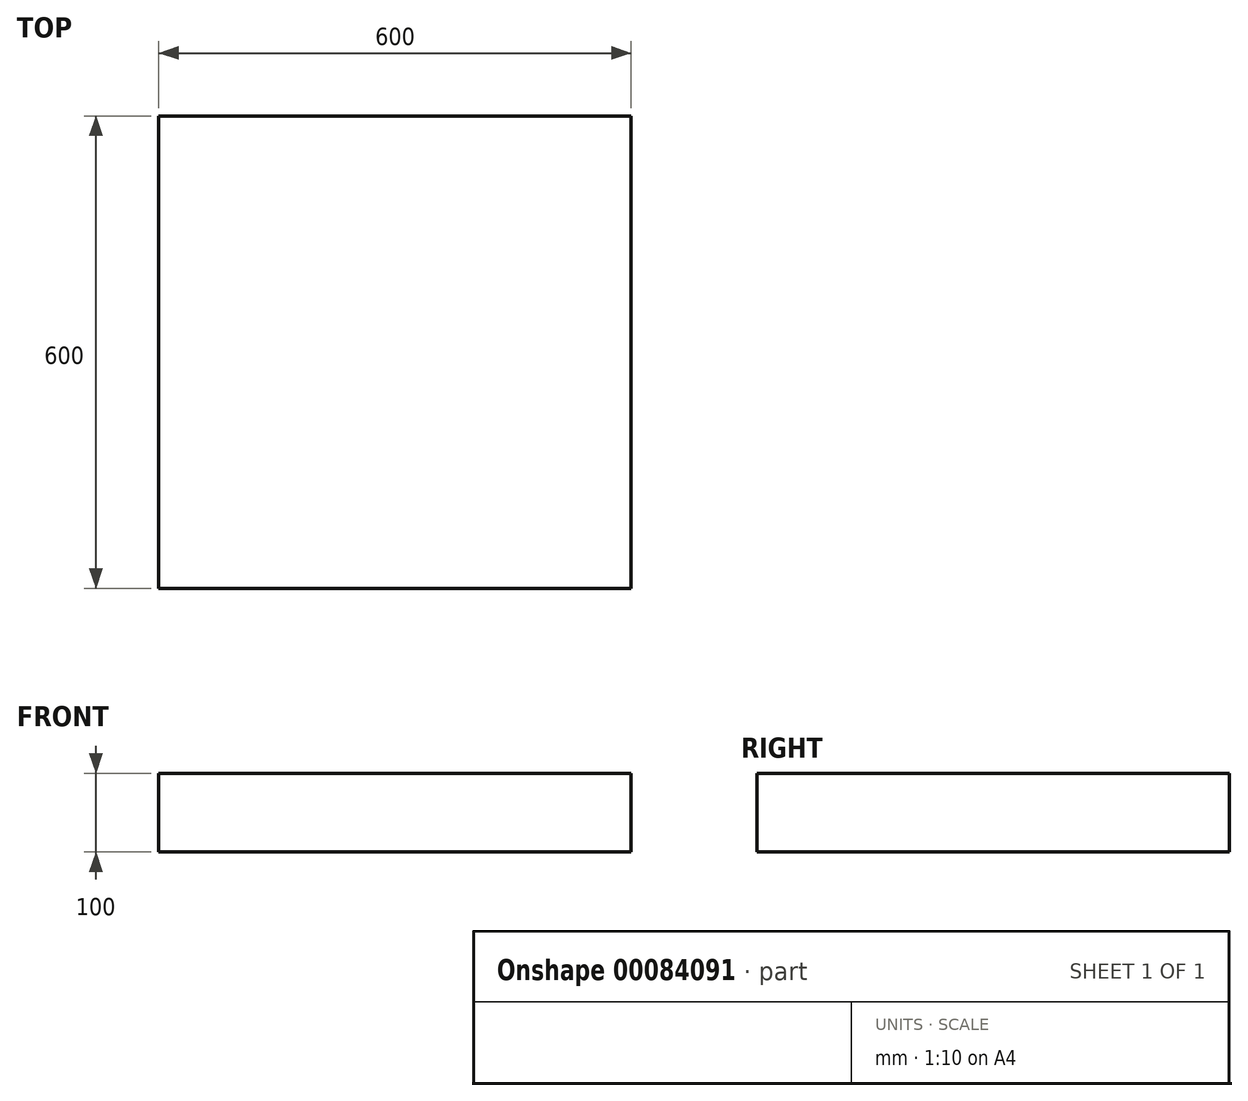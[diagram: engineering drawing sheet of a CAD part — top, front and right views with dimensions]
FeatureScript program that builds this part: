
annotation { "Feature Type Name" : "Feature", "Feature Type Description" : "" }
export const myFeature = defineFeature(function(context is Context, id is Id, definition is map)
    precondition{}
    {
        {
            var Q0;
            Q0=qCreatedBy(makeId("Top.planeOp"),FACE);
            var sketch = newSketch(context, id + "F0", { "sketchPlane" : qUnion([Q0])});
            skLineSegment(sketch, "E0.bottom", {"start": v(0, 600) * mm, "end": v(600, 600) * mm});
            skLineSegment(sketch, "E0.top", {"start": v(0, 0) * mm, "end": v(600, 0) * mm});
            skLineSegment(sketch, "E0.left", {"start": v(0, 600) * mm, "end": v(0, 0) * mm});
            skLineSegment(sketch, "E0.right", {"start": v(600, 600) * mm, "end": v(600, 0) * mm});
            skSolve(sketch);
        }
        {
            var Q0;
            Q0 = qSketchRegion(id + "F0", true);
            extrude(context, id + "F1", {"entities" : qUnion([Q0]), "depth" : 100 * mm});
        }
    });
